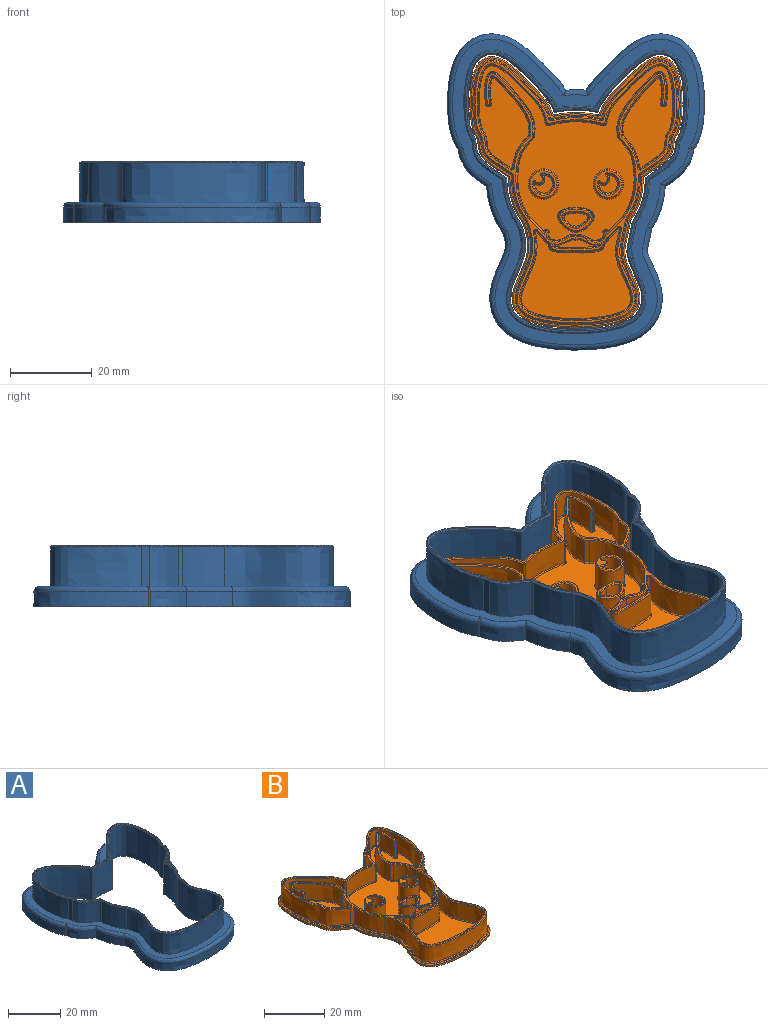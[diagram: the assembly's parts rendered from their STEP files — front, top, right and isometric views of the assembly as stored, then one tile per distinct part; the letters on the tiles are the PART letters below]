
ASSEMBLY  parts=2 mates=1
PART A: 69 faces, bbox 63.4x77.8x15.3 mm
  f0: extruded ~9.7x6.59mm, area 88.8mm2, adj f9,f32,f40,f66
  f1: extruded ~10.01x9.7mm, area 103.3mm2, adj f2,f32,f38,f66
  f2: extruded ~34.19x27.16mm, area 788.5mm2, adj f1,f3,f32,f36
  f3: extruded ~10.45x9.7mm, area 108.4mm2, adj f2,f32,f34,f65
  f4: extruded ~9.7x7.17mm, area 99.4mm2, adj f5,f32,f33,f65
  f5: extruded ~9.7x2.02mm, area 19.7mm2, adj f4,f32,f35,f67
  f6: extruded ~22.54x22.33mm, area 456.1mm2, adj f32,f37,f63,f67
  f7: extruded ~9.7x7.82mm, area 76.1mm2, adj f32,f39,f63,f64
  f8: extruded ~22.54x22.32mm, area 455.9mm2, adj f32,f41,f64,f68
  f9: extruded ~9.7x3.08mm, area 30.3mm2, adj f0,f32,f42,f68
  f10: extruded ~21.19x20.81mm, area 668.2mm2, adj f11,f19,f21,f47
  f11: extruded ~14.7x10.63mm, area 157.4mm2, adj f10,f12,f21,f49
  f12: extruded ~21.19x20.82mm, area 668.4mm2, adj f11,f13,f21,f51
  f13: extruded ~14.7x2.28mm, area 33.7mm2, adj f12,f14,f21,f52
  f14: extruded ~14.7x7.35mm, area 154.7mm2, adj f13,f15,f21,f50
  f15: extruded ~14.7x11.01mm, area 172.3mm2, adj f14,f16,f21,f48
  f16: extruded ~32.19x26.53mm, area 1159.5mm2, adj f15,f17,f21,f46
  f17: extruded ~14.7x10.69mm, area 166.6mm2, adj f16,f18,f21,f44
  f18: extruded ~14.7x7.09mm, area 140.9mm2, adj f17,f19,f21,f43
  f19: extruded ~14.7x3.19mm, area 47.8mm2, adj f10,f18,f21,f45
  f20: plane 69.51x54.89mm, normal (0,0,1), area 109.8mm2, adj f33,f34,f35,f36,f37,f38,f39,f40
  f21: plane 77.5x63.01mm, normal (0,0,-1), area 1206.2mm2, adj f10,f11,f12,f13,f14,f15,f16,f17
  f22: extruded ~29.09x28.11mm, area 215.2mm2, adj f21,f23,f31,f62
  f23: extruded ~4.83x3.75mm, area 18.1mm2, adj f21,f22,f24,f61
  f24: extruded ~29.08x28.11mm, area 215.2mm2, adj f21,f23,f25,f59
  f25: plane 3.75x0.24mm, normal (0.8,-0.6,0), area 1.1mm2, adj f21,f24,f26,f57
  f26: extruded ~9.01x6.94mm, area 44.2mm2, adj f21,f25,f27,f55
  f27: extruded ~10.37x3.75mm, area 41.2mm2, adj f21,f26,f28,f53
  f28: extruded ~42.21x29.69mm, area 341mm2, adj f21,f27,f29,f54
  f29: extruded ~11.26x3.9mm, area 45.2mm2, adj f21,f28,f30,f56
  f30: extruded ~8.96x6.94mm, area 44mm2, adj f21,f29,f31,f58
  f31: plane 3.75x0.29mm, normal (-0.83,-0.55,0), area 1.3mm2, adj f21,f22,f30,f60
  f32: plane 75x60.51mm, normal (0,0,1), area 655.3mm2, adj f0,f1,f2,f3,f4,f5,f6,f7
  f33: bspline ~8.52x8.3mm, area 4.6mm2, adj f4,f20,f34,f35,f65
  f34: bspline ~12.28x4.23mm, area 5mm2, adj f3,f20,f33,f36,f65
  f35: bspline ~2.39x0.54mm, area 0.9mm2, adj f5,f20,f33,f37
  f36: bspline ~34.34x29.45mm, area 34.2mm2, adj f2,f20,f34,f38
  f37: bspline ~23.84x22.67mm, area 20.3mm2, adj f6,f20,f35,f39,f63
  f38: bspline ~11.84x3.93mm, area 4.8mm2, adj f1,f20,f36,f40,f66
  f39: bspline ~10.84x1.07mm, area 4.3mm2, adj f7,f20,f37,f41,f63,f64
  f40: bspline ~8.01x7.41mm, area 4.1mm2, adj f0,f20,f38,f42,f66
  f41: bspline ~23.84x23.14mm, area 20.3mm2, adj f8,f20,f39,f42,f64
  f42: bspline ~3.49x0.87mm, area 1.3mm2, adj f9,f20,f40,f41
  f43: bspline ~7.95x7.19mm, area 4.1mm2, adj f18,f20,f44,f45
  f44: bspline ~10.88x3.47mm, area 4.8mm2, adj f17,f20,f43,f46
  f45: bspline ~3.48x0.85mm, area 1.4mm2, adj f19,f20,f43,f47
  f46: bspline ~32.95x28.97mm, area 33.5mm2, adj f16,f20,f44,f48
  f47: bspline ~22.17x21.87mm, area 19.5mm2, adj f10,f20,f45,f49
  f48: bspline ~11.19x3.69mm, area 5mm2, adj f15,f20,f46,f50
  f49: bspline ~10.75x0.87mm, area 4.5mm2, adj f11,f20,f47,f51
  f50: bspline ~8.2x8.2mm, area 4.5mm2, adj f14,f20,f48,f52
  f51: bspline ~22.18x21.84mm, area 19.5mm2, adj f12,f20,f49,f52
  f52: bspline ~2.55x0.6mm, area 1mm2, adj f13,f20,f50,f51
  f53: bspline ~19.8x5.53mm, area 22mm2, adj f27,f32,f54,f55
  f54: bspline ~42.31x30.62mm, area 174.7mm2, adj f28,f32,f53,f56
  f55: bspline ~31.72x29.24mm, area 23.3mm2, adj f26,f32,f53,f57
  f56: bspline ~15.74x6.66mm, area 24mm2, adj f29,f32,f54,f58
  f57: cylinder r=1.25mm len=1.37mm, axis (0.6,0.8,0), area 0.8mm2, adj f25,f32,f55,f59
  f58: bspline ~10.54x8.73mm, area 23.2mm2, adj f30,f32,f56,f60
  f59: bspline ~29.63x28.46mm, area 111.4mm2, adj f24,f32,f57,f61
  f60: cylinder r=1.25mm len=1.39mm, axis (0.55,-0.83,0), area 0.9mm2, adj f31,f32,f58,f62
  f61: bspline ~9.82x1.66mm, area 10.8mm2, adj f23,f32,f59,f62
  f62: bspline ~29.66x28.44mm, area 111.4mm2, adj f22,f32,f60,f61
  f63: cylinder r=1mm len=9.7mm, axis (0,0,-1), area 12.3mm2, adj f6,f7,f32,f37,f39
  f64: cylinder r=1mm len=9.7mm, axis (0,0,-1), area 12.3mm2, adj f7,f8,f32,f39,f41
  f65: cylinder r=1mm len=9.7mm, axis (0,0,-1), area 9.2mm2, adj f3,f4,f32,f33,f34
  f66: cylinder r=1mm len=9.7mm, axis (0,0,-1), area 9.2mm2, adj f0,f1,f32,f38,f40
  f67: cylinder r=1mm len=9.7mm, axis (0,0,-1), area 0.1mm2, adj f5,f6,f32
  f68: cylinder r=1mm len=9.7mm, axis (0,0,-1), area 0.3mm2, adj f8,f9,f32
PART B: 257 faces, bbox 52.3x66.8x8.3 mm
  f0: plane 47.51x42.72mm, normal (0,0,1), area 945.7mm2, adj f190,f191,f192,f193,f194,f195,f196,f198
  f1: extruded ~29.46x20.23mm, area 39.5mm2, adj f2,f8,f89,f164
  f2: extruded ~11.03x3.32mm, area 8.2mm2, adj f1,f3,f8,f162
  f3: extruded ~31.19x26.21mm, area 54.4mm2, adj f2,f4,f8,f160
  f4: extruded ~10.78x3.14mm, area 8mm2, adj f3,f5,f8,f158
  f5: extruded ~29.46x20.22mm, area 39.5mm2, adj f4,f8,f88,f159
  f6: extruded ~10.6x0.7mm, area 7.5mm2, adj f8,f88,f89,f163
  f7: plane 65.9x51.41mm, normal (0,0,1), area 89.9mm2, adj f158,f159,f160,f161,f162,f163,f164,f165
  f8: plane 66.51x52.02mm, normal (0,0,-1), area 2144mm2, adj f1,f2,f3,f4,f5,f6,f88,f89
  f9: extruded ~6.75x5.65mm, area 40.4mm2, adj f10,f52,f54,f154
  f10: extruded ~11.08x6.75mm, area 78.1mm2, adj f9,f52,f54,f155
  f11: plane 6.45x2.4mm, normal (0.7,-0.72,0), area 21.6mm2, adj f49,f79,f136,f172
  f12: extruded ~27.23x22.12mm, area 427.8mm2, adj f79,f80,f140,f171
  f13: plane 6.45x1.69mm, normal (-0.7,-0.72,0), area 15.2mm2, adj f14,f80,f141,f167
  f14: extruded ~6.45x1.48mm, area 13.9mm2, adj f13,f15,f139,f166
  f15: extruded ~12.97x6.45mm, area 99mm2, adj f14,f49,f137,f168
  f16: extruded ~13.6x6.5mm, area 89.6mm2, adj f72,f75,f95,f198
  f17: extruded ~25.16x16.69mm, area 323.8mm2, adj f18,f72,f96,f194
  f18: extruded ~6.5x0.39mm, area 3mm2, adj f17,f78,f98,f192
  f19: extruded ~7.7x6.5mm, area 57.5mm2, adj f20,f78,f102,f191
  f20: extruded ~6.5x1.52mm, area 10mm2, adj f19,f21,f104,f193
  f21: extruded ~13.05x9.9mm, area 150.7mm2, adj f20,f77,f106,f195,f197,f199
  f22: plane 6.5x0.2mm, normal (-0.22,-0.98,0), area 1.3mm2, adj f76,f77,f110,f203
  f23: extruded ~16.07x11.91mm, area 186.1mm2, adj f24,f76,f114,f207
  f24: extruded ~6.5x0.76mm, area 6.9mm2, adj f23,f25,f116,f209
  f25: extruded ~7.77x6.5mm, area 55.9mm2, adj f24,f26,f118,f211
  f26: extruded ~11.06x6.5mm, area 76.2mm2, adj f25,f27,f120,f213
  f27: plane 6.5x3.28mm, normal (-0.7,0.72,0), area 29.8mm2, adj f26,f122,f157,f215
  f28: plane 6.5x0.2mm, normal (-0.13,0.99,0), area 1.3mm2, adj f81,f82,f128,f221
  f29: extruded ~6.91x6.5mm, area 55.9mm2, adj f30,f82,f132,f225
  f30: extruded ~6.91x6.5mm, area 55.9mm2, adj f29,f83,f134,f227
  f31: plane 6.5x0.2mm, normal (0.13,0.99,0), area 1.3mm2, adj f83,f84,f131,f231
  f32: plane 6.5x3.28mm, normal (0.7,0.72,0), area 29.8mm2, adj f33,f125,f156,f232
  f33: extruded ~11.06x6.5mm, area 76.2mm2, adj f32,f34,f123,f230
  f34: extruded ~7.77x6.5mm, area 55.9mm2, adj f33,f35,f121,f228
  f35: extruded ~6.5x0.76mm, area 6.9mm2, adj f34,f36,f119,f226
  f36: extruded ~16.07x11.91mm, area 186.1mm2, adj f35,f87,f117,f224
  f37: plane 6.5x0.2mm, normal (0.22,-0.98,0), area 1.3mm2, adj f86,f87,f113,f220
  f38: extruded ~13.05x9.9mm, area 150.7mm2, adj f39,f86,f109,f212,f214,f216
  f39: extruded ~6.5x1.52mm, area 10mm2, adj f38,f40,f107,f210
  f40: extruded ~7.7x6.5mm, area 57.5mm2, adj f39,f85,f105,f208
  f41: extruded ~6.5x0.39mm, area 3mm2, adj f50,f85,f101,f204
  f42: extruded ~6.45x0.97mm, area 7.5mm2, adj f43,f51,f144,f180
  f43: extruded ~27.33x18.51mm, area 344.5mm2, adj f42,f73,f146,f182
  f44: extruded ~12.02x6.45mm, area 78.3mm2, adj f73,f74,f150,f181
  f45: extruded ~27.33x18.51mm, area 344.6mm2, adj f46,f74,f151,f177
  f46: extruded ~6.45x0.97mm, area 7.5mm2, adj f45,f47,f149,f175
  f47: extruded ~11.06x6.45mm, area 75.7mm2, adj f46,f48,f147,f174
  f48: extruded ~29.19x25.58mm, area 485.3mm2, adj f47,f51,f145,f176
  f49: extruded ~6.45x1.43mm, area 12.7mm2, adj f11,f15,f135,f170
  f50: extruded ~25.16x16.69mm, area 323.8mm2, adj f41,f75,f99,f202
  f51: extruded ~10.93x6.45mm, area 74.7mm2, adj f42,f48,f143,f178
  f52: extruded ~6.75x5.42mm, area 38.8mm2, adj f9,f10,f54,f153
  f53: plane 64.4x49.85mm, normal (0,0,1), area 233.4mm2, adj f94,f95,f96,f97,f98,f99,f100,f101
  f54: plane 11.68x2.21mm, normal (0,0,1), area 12.5mm2, adj f9,f10,f52
  f55: plane 26.7x22.01mm, normal (0,0,1), area 389.8mm2, adj f166,f167,f168,f169,f170,f171,f172,f173
  f56: extruded ~6.5x5.7mm, area 72.6mm2, adj f59,f90,f238
  f57: extruded ~6.45x3.7mm, area 51.6mm2, adj f58,f93,f189
  f58: extruded ~6.45x3.7mm, area 51.6mm2, adj f57,f92,f188
  f59: extruded ~6.5x5.7mm, area 72.6mm2, adj f56,f91,f237
  f60: plane 8.3x5.51mm, normal (0,0,1), area 9.1mm2, adj f90,f91,f92,f93
  f61: plane 5.81x3.1mm, normal (0,0,1), area 12.9mm2, adj f188,f189
  f62: cylinder r=1.2mm len=6.45mm, axis (0,0,-1), area 27.1mm2, adj f187,f243,f245,f253
  f63: cylinder r=2.5mm len=6.45mm, axis (0,0,-1), area 82mm2, adj f186,f243,f245,f254
  f64: cylinder r=3.5mm len=7mm, axis (0,0,-1), area 142.9mm2, adj f236,f256
  f65: plane 6.5x6.5mm, normal (0,0,1), area 12.9mm2, adj f252,f253,f254,f255,f256
  f66: plane 4.4x4.4mm, normal (0,0,1), area 10.7mm2, adj f186,f187
  f67: cylinder r=1.24mm len=6.45mm, axis (0,0,-1), area 26.8mm2, adj f185,f239,f241,f248
  f68: cylinder r=2.5mm len=6.45mm, axis (0,0,-1), area 81.1mm2, adj f184,f239,f241,f249
  f69: cylinder r=3.5mm len=7mm, axis (0,0,-1), area 142.9mm2, adj f235,f251
  f70: plane 6.5x6.5mm, normal (0,0,1), area 13mm2, adj f247,f248,f249,f250,f251
  f71: plane 4.4x4.4mm, normal (0,0,1), area 10.7mm2, adj f184,f185
  f72: cylinder r=0.4mm len=6.5mm, axis (0,0,-1), area 4.5mm2, adj f16,f17,f94,f196
  f73: cylinder r=0.4mm len=6.45mm, axis (0,0,-1), area 4.1mm2, adj f43,f44,f148,f183
  f74: cylinder r=0.4mm len=6.45mm, axis (0,0,-1), area 4.1mm2, adj f44,f45,f152,f179
  f75: cylinder r=0.4mm len=6.5mm, axis (0,0,-1), area 4.5mm2, adj f16,f50,f97,f200
  f76: cylinder r=0.4mm len=6.5mm, axis (0,0,-1), area 4.2mm2, adj f22,f23,f112,f205
  f77: cylinder r=0.4mm len=6.5mm, axis (0,0,-1), area 4mm2, adj f21,f22,f108,f201
  f78: cylinder r=0.4mm len=6.5mm, axis (0,0,-1), area 5.3mm2, adj f18,f19,f100,f190
  f79: cylinder r=0.4mm len=6.45mm, axis (0,0,-1), area 6.6mm2, adj f11,f12,f138,f173
  f80: cylinder r=0.4mm len=6.45mm, axis (0,0,-1), area 6.6mm2, adj f12,f13,f142,f169
  f81: cylinder r=0.4mm len=6.5mm, axis (0,0,-1), area 2.4mm2, adj f28,f126,f157,f219
  f82: cylinder r=0.4mm len=6.5mm, axis (0,0,-1), area 4.1mm2, adj f28,f29,f130,f223
  f83: cylinder r=0.4mm len=6.5mm, axis (0,0,-1), area 4.1mm2, adj f30,f31,f133,f229
  f84: cylinder r=0.4mm len=6.5mm, axis (0,0,-1), area 2.4mm2, adj f31,f129,f156,f233
  f85: cylinder r=0.4mm len=6.5mm, axis (0,0,-1), area 5.3mm2, adj f40,f41,f103,f206
  f86: cylinder r=0.4mm len=6.5mm, axis (0,0,-1), area 4mm2, adj f37,f38,f111,f218
  f87: cylinder r=0.4mm len=6.5mm, axis (0,0,-1), area 4.2mm2, adj f36,f37,f115,f222
  f88: cylinder r=0.4mm len=0.7mm, axis (0,0,-1), area 0.4mm2, adj f5,f6,f8,f161
  f89: cylinder r=0.4mm len=0.7mm, axis (0,0,-1), area 0.4mm2, adj f1,f6,f8,f165
  f90: bspline ~5.7x4.22mm, area 3.8mm2, adj f56,f60,f91
  f91: bspline ~5.7x4.22mm, area 3.8mm2, adj f59,f60,f90
  f92: bspline ~4.2x3.47mm, area 3mm2, adj f58,f60,f93
  f93: bspline ~4.2x3.47mm, area 3mm2, adj f57,f60,f92
  f94: cone r=0.15mm half-angle=45deg, axis (0,0,-1), area 0.2mm2, adj f53,f72,f95,f96
  f95: bspline ~13.73x1.26mm, area 4.9mm2, adj f16,f53,f94,f97
  f96: bspline ~25.67x17.2mm, area 17.8mm2, adj f17,f53,f94,f98
  f97: cone r=0.15mm half-angle=45deg, axis (0,0,-1), area 0.2mm2, adj f53,f75,f95,f99
  f98: bspline ~0.53x0.47mm, area 0.2mm2, adj f18,f53,f96,f100
  f99: bspline ~25.71x17.21mm, area 17.9mm2, adj f50,f53,f97,f101
  f100: cone r=0.65mm half-angle=45deg, axis (0,0,1), area 0.4mm2, adj f53,f78,f98,f102
  f101: bspline ~0.53x0.47mm, area 0.2mm2, adj f41,f53,f99,f103
  f102: bspline ~8.09x4.42mm, area 3.1mm2, adj f19,f53,f100,f104
  f103: cone r=0.65mm half-angle=45deg, axis (0,0,1), area 0.4mm2, adj f53,f85,f101,f105
  f104: bspline ~1.65x0.45mm, area 0.6mm2, adj f20,f53,f102,f106
  f105: bspline ~8.09x4.42mm, area 3.1mm2, adj f40,f53,f103,f107
  f106: bspline ~13.32x10.46mm, area 8.3mm2, adj f21,f53,f104,f108
  f107: bspline ~1.73x0.46mm, area 0.6mm2, adj f39,f53,f105,f109
  f108: cone r=0.15mm half-angle=45deg, axis (0,0,-1), area 0.1mm2, adj f53,f77,f106,f110
  f109: bspline ~13.33x10.46mm, area 8.4mm2, adj f38,f53,f107,f111
  f110: plane 0.29x0.25mm, normal (-0.15,-0.69,0.71), area 0.1mm2, adj f22,f53,f108,f112
  f111: cone r=0.15mm half-angle=45deg, axis (0,0,-1), area 0.1mm2, adj f53,f86,f109,f113
  f112: cone r=0.15mm half-angle=45deg, axis (0,0,-1), area 0.2mm2, adj f53,f76,f110,f114
  f113: plane 0.29x0.25mm, normal (0.15,-0.69,0.71), area 0.1mm2, adj f37,f53,f111,f115
  f114: bspline ~17.47x11.92mm, area 9.9mm2, adj f23,f53,f112,f116
  f115: cone r=0.15mm half-angle=45deg, axis (0,0,-1), area 0.2mm2, adj f53,f87,f113,f117
  f116: bspline ~0.94x0.93mm, area 0.4mm2, adj f24,f53,f114,f118
  f117: bspline ~17.47x11.92mm, area 9.9mm2, adj f36,f53,f115,f119
  f118: bspline ~7.94x3.41mm, area 3.1mm2, adj f25,f53,f116,f120
  f119: bspline ~0.94x0.93mm, area 0.4mm2, adj f35,f53,f117,f121
  f120: bspline ~11.24x3.33mm, area 4.2mm2, adj f26,f53,f118,f122
  f121: bspline ~7.94x3.41mm, area 3.1mm2, adj f34,f53,f119,f123
  f122: plane 4.07x4.01mm, normal (-0.49,0.51,0.71), area 1.9mm2, adj f27,f53,f120,f124,f126,f157
  f123: bspline ~11.73x3.69mm, area 4.2mm2, adj f33,f53,f121,f125
  f124: bspline ~0.64x0.38mm, area 0.1mm2, adj f53,f122,f126
  f125: plane 4.07x4.01mm, normal (0.49,0.51,0.71), area 1.9mm2, adj f32,f53,f123,f127,f129,f156
  f126: cone r=0.15mm half-angle=45deg, axis (0,0,-1), area 0.2mm2, adj f53,f81,f122,f124,f128,f157
  f127: bspline ~0.64x0.38mm, area 0.1mm2, adj f53,f125,f129
  f128: plane 0.27x0.25mm, normal (-0.09,0.7,0.71), area 0.1mm2, adj f28,f53,f126,f130
  f129: cone r=0.15mm half-angle=45deg, axis (0,0,-1), area 0.2mm2, adj f53,f84,f125,f127,f131,f156
  f130: cone r=0.15mm half-angle=45deg, axis (0,0,-1), area 0.2mm2, adj f53,f82,f128,f132
  f131: plane 0.27x0.25mm, normal (0.09,0.7,0.71), area 0.1mm2, adj f31,f53,f129,f133
  f132: bspline ~7.68x2.42mm, area 3.1mm2, adj f29,f53,f130,f134
  f133: cone r=0.15mm half-angle=45deg, axis (0,0,-1), area 0.2mm2, adj f53,f83,f131,f134
  f134: bspline ~7.68x2.42mm, area 3.1mm2, adj f30,f53,f132,f133
  f135: bspline ~1.81x1.71mm, area 0.7mm2, adj f49,f53,f136,f137
  f136: plane 2.63x2.52mm, normal (0.49,-0.51,0.71), area 1.2mm2, adj f11,f53,f135,f138
  f137: bspline ~13.14x2.67mm, area 5.3mm2, adj f15,f53,f135,f139
  f138: cone r=0.65mm half-angle=45deg, axis (0,0,1), area 0.5mm2, adj f53,f79,f136,f140
  f139: bspline ~1.79x1.7mm, area 0.8mm2, adj f14,f53,f137,f141
  f140: bspline ~27.86x22.38mm, area 23.7mm2, adj f12,f53,f138,f142
  f141: plane 1.92x1.83mm, normal (-0.49,-0.51,0.71), area 0.8mm2, adj f13,f53,f139,f142
  f142: cone r=0.65mm half-angle=45deg, axis (0,0,1), area 0.5mm2, adj f53,f80,f140,f141
  f143: bspline ~11.12x3.34mm, area 4.1mm2, adj f51,f53,f144,f145
  f144: bspline ~1.22x0.94mm, area 0.4mm2, adj f42,f53,f143,f146
  f145: bspline ~29.41x27.68mm, area 26.5mm2, adj f48,f53,f143,f147
  f146: bspline ~27.38x18.52mm, area 18.7mm2, adj f43,f53,f144,f148
  f147: bspline ~12.28x3.78mm, area 4.1mm2, adj f47,f53,f145,f149
  f148: cone r=0.65mm half-angle=45deg, axis (0,0,1), area 0.3mm2, adj f53,f73,f146,f150
  f149: bspline ~1.28x0.97mm, area 0.4mm2, adj f46,f53,f147,f151
  f150: bspline ~12.02x1.01mm, area 4.3mm2, adj f44,f53,f148,f152
  f151: bspline ~27.39x18.53mm, area 18.7mm2, adj f45,f53,f149,f152
  f152: cone r=0.65mm half-angle=45deg, axis (0,0,1), area 0.3mm2, adj f53,f74,f150,f151
  f153: bspline ~6.29x1.69mm, area 2.1mm2, adj f52,f53,f154,f155
  f154: bspline ~6.49x1.69mm, area 2.1mm2, adj f9,f53,f153,f155
  f155: bspline ~11.57x1.25mm, area 4.3mm2, adj f10,f53,f153,f154
  f156: cylinder r=0.3mm len=6.5mm, axis (0,0,-1), area 3mm2, adj f32,f84,f125,f129,f234
  f157: cylinder r=0.3mm len=6.5mm, axis (0,0,-1), area 3mm2, adj f27,f81,f122,f126,f217
  f158: bspline ~15.09x4.9mm, area 5.4mm2, adj f4,f7,f159,f160
  f159: bspline ~29.86x20.37mm, area 26.7mm2, adj f5,f7,f158,f161
  f160: bspline ~31.3x26.73mm, area 36.4mm2, adj f3,f7,f158,f162
  f161: torus R=0.7mm, axis (0,0,1), area 0.4mm2, adj f7,f88,f159,f163
  f162: bspline ~14.01x4.04mm, area 5.5mm2, adj f2,f7,f160,f164
  f163: bspline ~11.61x0.99mm, area 5mm2, adj f6,f7,f161,f165
  f164: bspline ~29.96x20.37mm, area 26.5mm2, adj f1,f7,f162,f165
  f165: torus R=0.7mm, axis (0,0,1), area 0.4mm2, adj f7,f89,f163,f164
  f166: bspline ~2.05x1.93mm, area 1mm2, adj f14,f55,f167,f168
  f167: cylinder r=0.3mm len=1.9mm, axis (-0.72,0.7,0), area 1.1mm2, adj f13,f55,f166,f169
  f168: bspline ~13.71x2.8mm, area 7.3mm2, adj f15,f55,f166,f170
  f169: torus R=0.1mm, axis (0,0,1), area 0.4mm2, adj f55,f80,f167,f171
  f170: bspline ~1.98x1.73mm, area 0.9mm2, adj f49,f55,f168,f172
  f171: bspline ~27.29x22.99mm, area 31.1mm2, adj f12,f55,f169,f173
  f172: cylinder r=0.3mm len=2.61mm, axis (-0.72,-0.7,0), area 1.6mm2, adj f11,f55,f170,f173
  f173: torus R=0.1mm, axis (0,0,1), area 0.4mm2, adj f55,f79,f171,f172
  f174: bspline ~12.95x4.01mm, area 5.5mm2, adj f7,f47,f175,f176
  f175: bspline ~1.55x1.18mm, area 0.5mm2, adj f7,f46,f174,f177
  f176: bspline ~29.89x26.03mm, area 35.6mm2, adj f7,f48,f174,f178
  f177: bspline ~33.33x19.13mm, area 25.4mm2, adj f7,f45,f175,f179
  f178: bspline ~12.05x3.94mm, area 5.4mm2, adj f7,f51,f176,f180
  f179: torus R=0.1mm, axis (0,0,1), area 0.2mm2, adj f7,f74,f177,f181
  f180: bspline ~1.55x1.18mm, area 0.5mm2, adj f7,f42,f178,f182
  f181: bspline ~13.31x1.22mm, area 5.7mm2, adj f7,f44,f179,f183
  f182: bspline ~33.33x19.19mm, area 25.4mm2, adj f7,f43,f180,f183
  f183: torus R=0.1mm, axis (0,0,1), area 0.2mm2, adj f7,f73,f181,f182
  f184: torus R=2.2mm, axis (0,0,1), area 5.5mm2, adj f68,f71,f240,f242
  f185: torus R=1.54mm, axis (0,0,1), area 2mm2, adj f67,f71,f240,f242
  f186: torus R=2.2mm, axis (0,0,1), area 5.6mm2, adj f63,f66,f244,f246
  f187: torus R=1.5mm, axis (0,0,1), area 2mm2, adj f62,f66,f244,f246
  f188: bspline ~3.93x3.7mm, area 3.6mm2, adj f58,f61,f189
  f189: bspline ~6.07x3.7mm, area 3.6mm2, adj f57,f61,f188
  f190: torus R=0.15mm, axis (0,0,1), area 0.2mm2, adj f0,f78,f191,f192
  f191: bspline ~9.1x4.47mm, area 3.5mm2, adj f0,f19,f190,f193
  f192: bspline ~0.73x0.6mm, area 0.2mm2, adj f0,f18,f190,f194
  f193: bspline ~1.99x0.5mm, area 0.6mm2, adj f0,f20,f191,f195
  f194: bspline ~28.63x16.75mm, area 19.4mm2, adj f0,f17,f192,f196
  f195: bspline ~17.07x9.23mm, area 6.4mm2, adj f0,f21,f193,f197
  f196: torus R=0.65mm, axis (0,0,1), area 0.3mm2, adj f0,f72,f194,f198
  f197: bspline ~0.27x0.25mm, area 0mm2, adj f21,f195,f199
  f198: bspline ~14.95x1.44mm, area 5.4mm2, adj f0,f16,f196,f200
  f199: bspline ~6.9x0.86mm, area 2.5mm2, adj f0,f21,f197,f201
  f200: torus R=0.65mm, axis (0,0,1), area 0.3mm2, adj f0,f75,f198,f202
  f201: torus R=0.65mm, axis (0,0,1), area 0.3mm2, adj f0,f77,f199,f203
  f202: bspline ~28.63x16.72mm, area 19.5mm2, adj f0,f50,f200,f204
  f203: cylinder r=0.25mm len=0.29mm, axis (-0.98,0.22,0), area 0.1mm2, adj f0,f22,f201,f205
  f204: bspline ~0.73x0.6mm, area 0.2mm2, adj f0,f41,f202,f206
  f205: torus R=0.65mm, axis (0,0,1), area 0.3mm2, adj f0,f76,f203,f207
  f206: torus R=0.15mm, axis (0,0,1), area 0.2mm2, adj f0,f85,f204,f208
  f207: bspline ~16.7x12.42mm, area 11.3mm2, adj f0,f23,f205,f209
  f208: bspline ~9.1x4.47mm, area 3.5mm2, adj f0,f40,f206,f210
  f209: bspline ~1.29x1.27mm, area 0.4mm2, adj f0,f24,f207,f211
  f210: bspline ~2.25x0.51mm, area 0.6mm2, adj f0,f39,f208,f212
  f211: bspline ~11.22x5.37mm, area 3.4mm2, adj f0,f25,f209,f213
  f212: bspline ~13.22x9.27mm, area 6.4mm2, adj f0,f38,f210,f214
  f213: bspline ~14.17x3.6mm, area 4.6mm2, adj f0,f26,f211,f215
  f214: bspline ~0.27x0.25mm, area 0mm2, adj f38,f212,f216
  f215: cylinder r=0.25mm len=3.46mm, axis (0.72,0.7,0), area 1.8mm2, adj f0,f27,f213,f217
  f216: bspline ~7x0.83mm, area 2.5mm2, adj f0,f38,f214,f218
  f217: torus R=0.05mm, axis (0,0,1), area 0.1mm2, adj f0,f157,f215,f219
  f218: torus R=0.65mm, axis (0,0,1), area 0.3mm2, adj f0,f86,f216,f220
  f219: torus R=0.65mm, axis (0,0,1), area 0.2mm2, adj f0,f81,f217,f221
  f220: cylinder r=0.25mm len=0.29mm, axis (-0.98,-0.22,0), area 0.1mm2, adj f0,f37,f218,f222
  f221: cylinder r=0.25mm len=0.27mm, axis (0.99,0.13,0), area 0.1mm2, adj f0,f28,f219,f223
  f222: torus R=0.65mm, axis (0,0,1), area 0.3mm2, adj f0,f87,f220,f224
  f223: torus R=0.65mm, axis (0,0,1), area 0.3mm2, adj f0,f82,f221,f225
  f224: bspline ~16.7x12.42mm, area 11.3mm2, adj f0,f36,f222,f226
  f225: bspline ~7.12x2.43mm, area 3.3mm2, adj f0,f29,f223,f227
  f226: bspline ~1.29x1.27mm, area 0.4mm2, adj f0,f35,f224,f228
  f227: bspline ~7.12x2.43mm, area 3.3mm2, adj f0,f30,f225,f229
  f228: bspline ~10.16x5.3mm, area 3.4mm2, adj f0,f34,f226,f230
  f229: torus R=0.65mm, axis (0,0,1), area 0.3mm2, adj f0,f83,f227,f231
  f230: bspline ~14.17x3.6mm, area 4.6mm2, adj f0,f33,f228,f232
  f231: cylinder r=0.25mm len=0.27mm, axis (0.99,-0.13,0), area 0.1mm2, adj f0,f31,f229,f233
  f232: cylinder r=0.25mm len=3.46mm, axis (0.72,-0.7,0), area 1.8mm2, adj f0,f32,f230,f234
  f233: torus R=0.65mm, axis (0,0,1), area 0.2mm2, adj f0,f84,f231,f234
  f234: torus R=0.05mm, axis (0,0,1), area 0.1mm2, adj f0,f156,f232,f233
  f235: torus R=3.75mm, axis (0,0,1), area 8.9mm2, adj f0,f69
  f236: torus R=3.75mm, axis (0,0,1), area 8.9mm2, adj f0,f64
  f237: bspline ~8.08x6.2mm, area 4.5mm2, adj f0,f59,f238
  f238: bspline ~6.6x6.2mm, area 4.5mm2, adj f0,f56,f237
  f239: cylinder r=0.15mm len=6.45mm, axis (0,0,-1), area 2.2mm2, adj f67,f68,f240,f247
  f240: bspline ~0.69x0.35mm, area 0.1mm2, adj f184,f185,f239
  f241: cylinder r=0.15mm len=6.45mm, axis (0,0,-1), area 2.2mm2, adj f67,f68,f242,f250
  f242: bspline ~0.69x0.35mm, area 0.1mm2, adj f184,f185,f241
  f243: cylinder r=0.15mm len=6.45mm, axis (0,0,-1), area 2.3mm2, adj f62,f63,f244,f252
  f244: bspline ~0.74x0.4mm, area 0.1mm2, adj f186,f187,f243
  f245: cylinder r=0.15mm len=6.45mm, axis (0,0,-1), area 2.3mm2, adj f62,f63,f246,f255
  f246: bspline ~0.74x0.4mm, area 0.1mm2, adj f186,f187,f245
  f247: cone r=0.4mm half-angle=45deg, axis (0,0,1), area 0.2mm2, adj f70,f239,f248,f249
  f248: cone r=0.99mm half-angle=45deg, axis (0,0,-1), area 1.3mm2, adj f67,f70,f247,f250
  f249: cone r=2.5mm half-angle=45deg, axis (0,0,1), area 4.7mm2, adj f68,f70,f247,f250
  f250: cone r=0.4mm half-angle=45deg, axis (0,0,1), area 0.2mm2, adj f70,f241,f248,f249
  f251: cone r=3.25mm half-angle=45deg, axis (0,0,-1), area 7.5mm2, adj f69,f70
  f252: cone r=0.4mm half-angle=45deg, axis (0,0,1), area 0.2mm2, adj f65,f243,f253,f254
  f253: cone r=0.95mm half-angle=45deg, axis (0,0,-1), area 1.3mm2, adj f62,f65,f252,f255
  f254: cone r=2.5mm half-angle=45deg, axis (0,0,1), area 4.7mm2, adj f63,f65,f252,f255
  f255: cone r=0.4mm half-angle=45deg, axis (0,0,1), area 0.2mm2, adj f65,f245,f253,f254
  f256: cone r=3.25mm half-angle=45deg, axis (0,0,-1), area 7.5mm2, adj f64,f65
PLACE A at identity
PLACE B t=(-0.01,-0.09,0)mm
MATE fastened B.f8 <-> A.f21  axis (0,0,-1) through (0,22.32,0)mm
